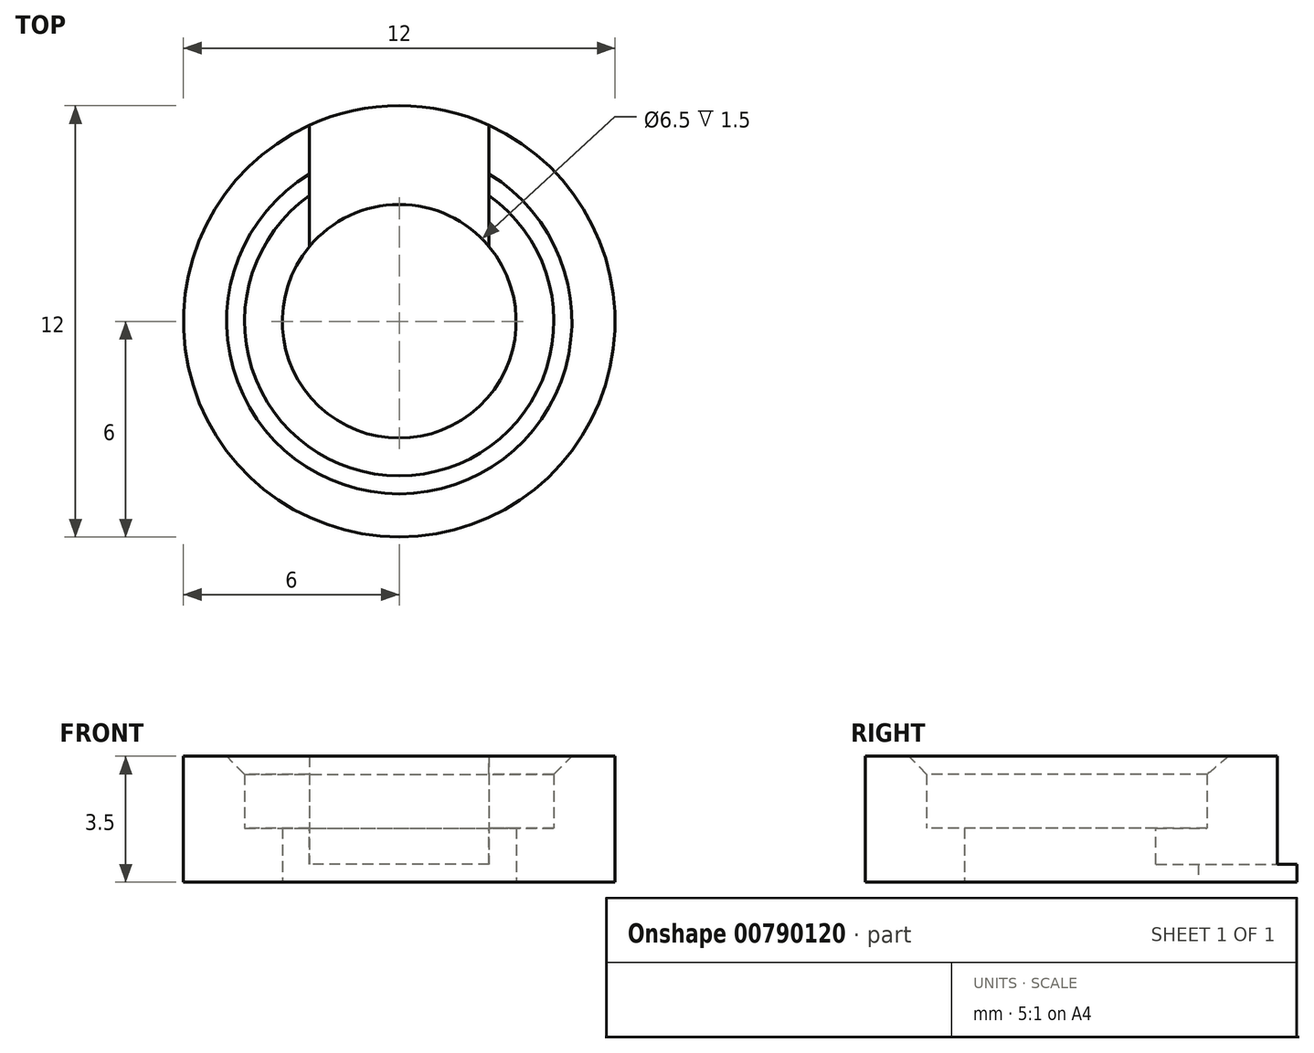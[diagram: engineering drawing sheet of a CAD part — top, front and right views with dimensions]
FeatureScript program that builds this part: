
annotation { "Feature Type Name" : "Feature", "Feature Type Description" : "" }
export const myFeature = defineFeature(function(context is Context, id is Id, definition is map)
    precondition{}
    {
        {
            var Q0;
            Q0=qCreatedBy(makeId("Top.planeOp"),FACE);
            var sketch = newSketch(context, id + "F0", { "sketchPlane" : qUnion([Q0])});
            skCircle(sketch, "E0", {"center": v(0, 0) * mm, "radius": 3.25 * mm});
            skCircle(sketch, "E1", {"center": v(0, 0) * mm, "radius": 6 * mm});
            skSolve(sketch);
        }
        {
            var Q0;
            Q0=makeQuery(id+"F0.imprint","IMPRINT",FACE,{"disambiguationData":[TD([[makeQuery(id+"F0.imprint","IMPRINT",EDGE,{"derivedFrom":sQuery(id+"F0.wireOp",EDGE,"E0")}),-1.0]])]});
            extrude(context, id + "F1", {"entities" : qUnion([Q0]), "depth" : 1.5 * mm});
        }
        {
            var Q0;
            Q0=makeQuery(id+"F1.opExtrude","CAP_FACE",FACE,{"disambiguationData":[OSD([sQuery(id+"F0.wireOp",EDGE,"E0"),sQuery(id+"F0.wireOp",EDGE,"E1")])],"isStart":false});
            var sketch = newSketch(context, id + "F2", { "sketchPlane" : qUnion([Q0])});
            skCircle(sketch, "E2.0", {"center": v(0, 0) * mm, "radius": 6 * mm});
            skCircle(sketch, "E3", {"center": v(0, 0) * mm, "radius": 4.3 * mm});
            skSolve(sketch);
        }
        {
            var Q0;
            Q0=makeQuery(id+"F2.imprint","IMPRINT",FACE,{"disambiguationData":[TD([[makeQuery(id+"F2.imprint","IMPRINT",EDGE,{"derivedFrom":sQuery(id+"F2.wireOp",EDGE,"E2.0")}),1.0]])]});
            extrude(context, id + "F3", {"entities" : qUnion([Q0]), "operationType" : NewBodyOperationType.ADD, "depth" : 2 * mm, "offsetDistance" : 25 * mm});
        }
        {
            var Q0;
            Q0=makeQuery(id+"F3.opExtrude","CAP_FACE",FACE,{"disambiguationData":[OSD([sQuery(id+"F2.wireOp",EDGE,"E2.0"),sQuery(id+"F2.wireOp",EDGE,"E3")])],"isStart":false});
            var sketch = newSketch(context, id + "F4", { "sketchPlane" : qUnion([Q0])});
            skLineSegment(sketch, "E4.bottom", {"start": v(-2.5, 2.08) * mm, "end": v(2.5, 2.08) * mm});
            skLineSegment(sketch, "E4.top", {"start": v(-2.5, 6) * mm, "end": v(2.5, 6) * mm});
            skLineSegment(sketch, "E4.left", {"start": v(-2.5, 2.08) * mm, "end": v(-2.5, 6) * mm});
            skLineSegment(sketch, "E4.right", {"start": v(2.5, 2.08) * mm, "end": v(2.5, 6) * mm});
            skPoint(sketch, "E4.middle", {"position": v(0, 4.04) * mm});
            skSolve(sketch);
        }
        {
            var Q0;
            Q0=qSketchRegion(id+"F4",true);
            var Q1;
            Q1=makeQuery(id+"F1.opExtrude","CAP_FACE",FACE,{"disambiguationData":[OSD([sQuery(id+"F0.wireOp",EDGE,"E0"),sQuery(id+"F0.wireOp",EDGE,"E1")])],"isStart":false});
            extrude(context, id + "F5", {"entities" : qUnion([Q0]), "operationType" : NewBodyOperationType.REMOVE, "oppositeDirection" : true, "endBoundEntityFace" : qUnion([Q1]), "depth" : 3 * mm});
        }
        {
            var Q0;
            Q0=makeQuery(id+"F3.opExtrude","CAP_EDGE",EDGE,{"disambiguationData":[OSD([sQuery(id+"F2.wireOp",EDGE,"E3")])],"isStart":false});
            chamfer(context, id + "F6", {"entities" : qUnion([Q0]), "width" : 0.5 * mm, "tangentPropagation" : true});
        }
    });
